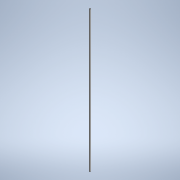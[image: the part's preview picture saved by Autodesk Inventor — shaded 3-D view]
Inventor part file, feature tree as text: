
AUTODESK INVENTOR PART (.ipt)
format: ipt  version: 2021 (Build 250183000, 183)  size: 93,184 bytes
history: native  units: mm
features: extrude x1, sketch x1
ambient origin geometry x8: Origin, YZ Plane, XZ Plane, XY Plane, X Axis, Y Axis, Z Axis, Center Point
bodies: Solid1 (feature_tree)
feature tree (2):
  extrude  "Extrusion1"  Depth=13.0mm
  sketch  "Sketch1"  dims[d0=13.0mm d1=13.0mm d2=1944.0mm d3=0.0mm]
